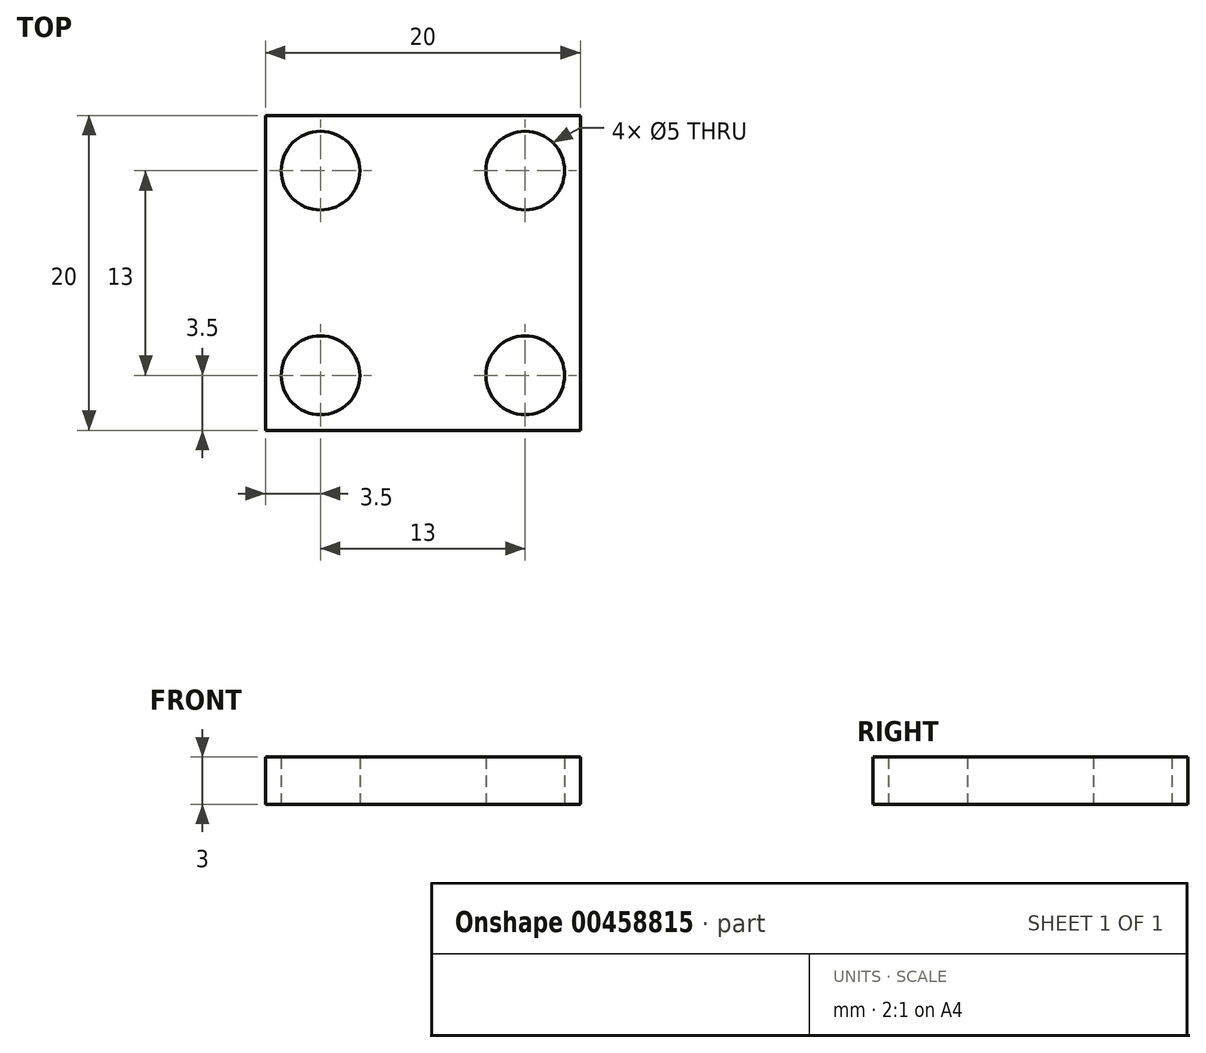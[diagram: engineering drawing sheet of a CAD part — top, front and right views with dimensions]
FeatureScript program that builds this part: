
annotation { "Feature Type Name" : "Feature", "Feature Type Description" : "" }
export const myFeature = defineFeature(function(context is Context, id is Id, definition is map)
    precondition{}
    {
        {
            var Q0;
            Q0=qCreatedBy(makeId("Top.planeOp"),FACE);
            var sketch = newSketch(context, id + "F0", { "sketchPlane" : qUnion([Q0])});
            skLineSegment(sketch, "E0.bottom", {"start": v(10, 10) * mm, "end": v(-10, 10) * mm});
            skLineSegment(sketch, "E0.top", {"start": v(10, -10) * mm, "end": v(-10, -10) * mm});
            skLineSegment(sketch, "E0.left", {"start": v(10, 10) * mm, "end": v(10, -10) * mm});
            skLineSegment(sketch, "E0.right", {"start": v(-10, 10) * mm, "end": v(-10, -10) * mm});
            skCircle(sketch, "E1", {"center": v(-6.5, 6.5) * mm, "radius": 2.5 * mm});
            skCircle(sketch, "E2.MirrorC", {"center": v(6.5, 6.5) * mm, "radius": 2.5 * mm});
            skCircle(sketch, "E3.MirrorC", {"center": v(-6.5, -6.5) * mm, "radius": 2.5 * mm});
            skCircle(sketch, "E4.MirrorC", {"center": v(6.5, -6.5) * mm, "radius": 2.5 * mm});
            skSolve(sketch);
        }
        {
            var Q0;
            Q0 = qSketchRegion(id + "F0", true);
            extrude(context, id + "F1", {"entities" : qUnion([Q0]), "depth" : 3 * mm, "offsetDistance" : 25 * mm});
        }
    });
